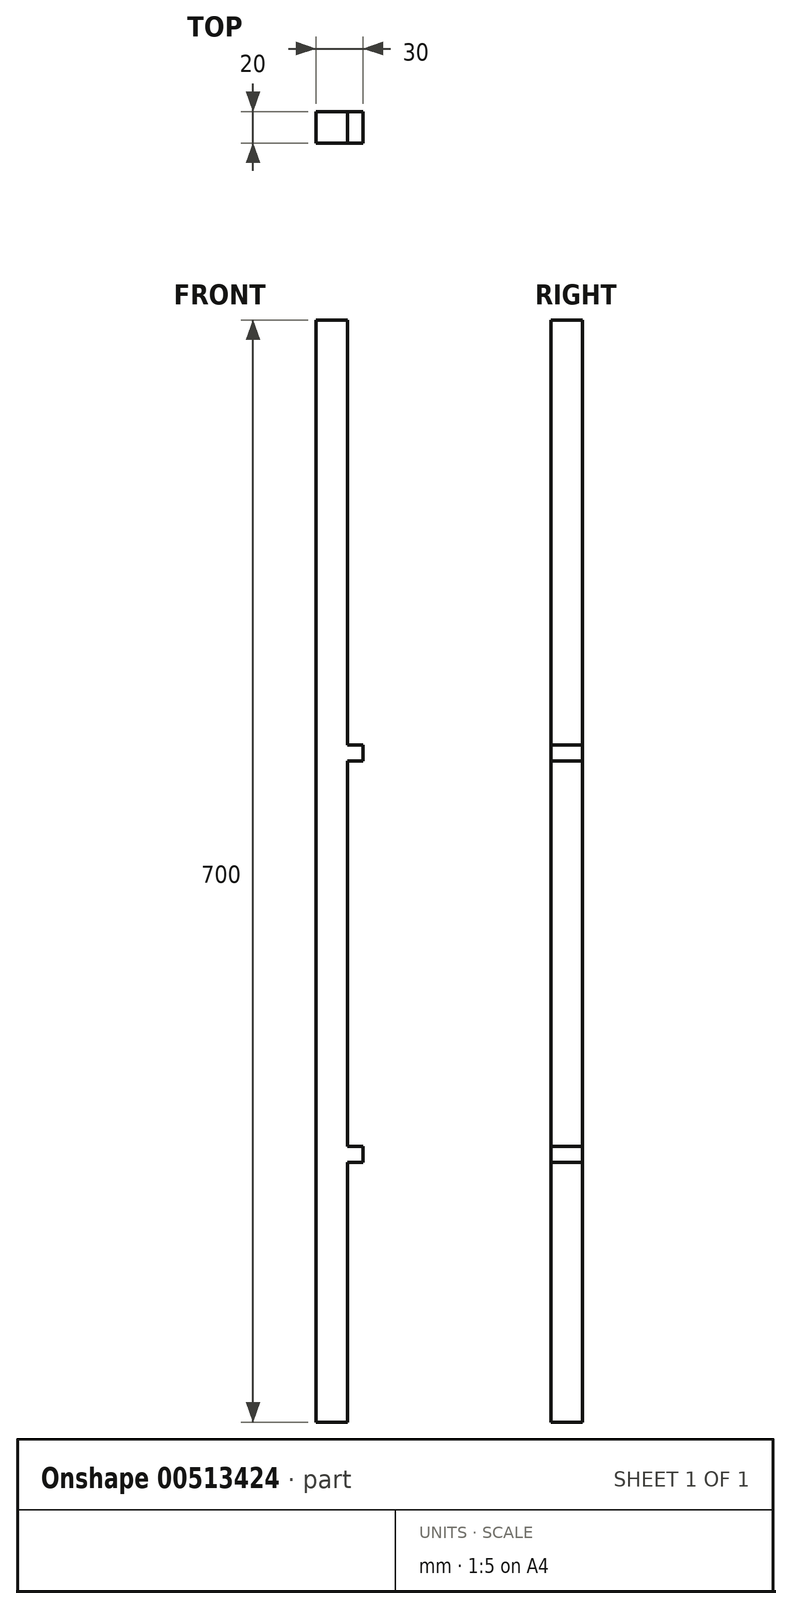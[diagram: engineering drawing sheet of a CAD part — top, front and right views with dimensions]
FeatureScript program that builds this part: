
annotation { "Feature Type Name" : "Feature", "Feature Type Description" : "" }
export const myFeature = defineFeature(function(context is Context, id is Id, definition is map)
    precondition{}
    {
        {
            var Q0;
            Q0=qCreatedBy(makeId("Front.planeOp"),FACE);
            var sketch = newSketch(context, id + "F0", { "sketchPlane" : qUnion([Q0])});
            skLineSegment(sketch, "E0", {"start": v(0, 0) * mm, "end": v(0, 700) * mm});
            skLineSegment(sketch, "E1", {"start": v(0, 700) * mm, "end": v(20, 700) * mm});
            skLineSegment(sketch, "E2", {"start": v(20, 700) * mm, "end": v(20, 430) * mm});
            skLineSegment(sketch, "E3", {"start": v(20, 430) * mm, "end": v(30, 430) * mm});
            skLineSegment(sketch, "E4", {"start": v(30, 430) * mm, "end": v(30, 420) * mm});
            skLineSegment(sketch, "E5", {"start": v(30, 420) * mm, "end": v(20, 420) * mm});
            skLineSegment(sketch, "E6", {"start": v(20, 420) * mm, "end": v(20, 175) * mm});
            skLineSegment(sketch, "E7", {"start": v(20, 175) * mm, "end": v(30, 175) * mm});
            skLineSegment(sketch, "E8", {"start": v(30, 175) * mm, "end": v(30, 165) * mm});
            skLineSegment(sketch, "E9", {"start": v(30, 165) * mm, "end": v(20, 165) * mm});
            skLineSegment(sketch, "E10", {"start": v(20, 165) * mm, "end": v(20, 0) * mm});
            skLineSegment(sketch, "E11", {"start": v(20, 0) * mm, "end": v(0, 0) * mm});
            skSolve(sketch);
        }
        {
            var Q0;
            Q0=makeQuery(id+"F0.imprint","IMPRINT",FACE,{"disambiguationData":[TD([[makeQuery(id+"F0.imprint","IMPRINT",EDGE,{"derivedFrom":sQuery(id+"F0.wireOp",EDGE,"E0")}),-1.0]])]});
            extrude(context, id + "F1", {"entities" : qUnion([Q0]), "depth" : 20 * mm});
        }
    });
